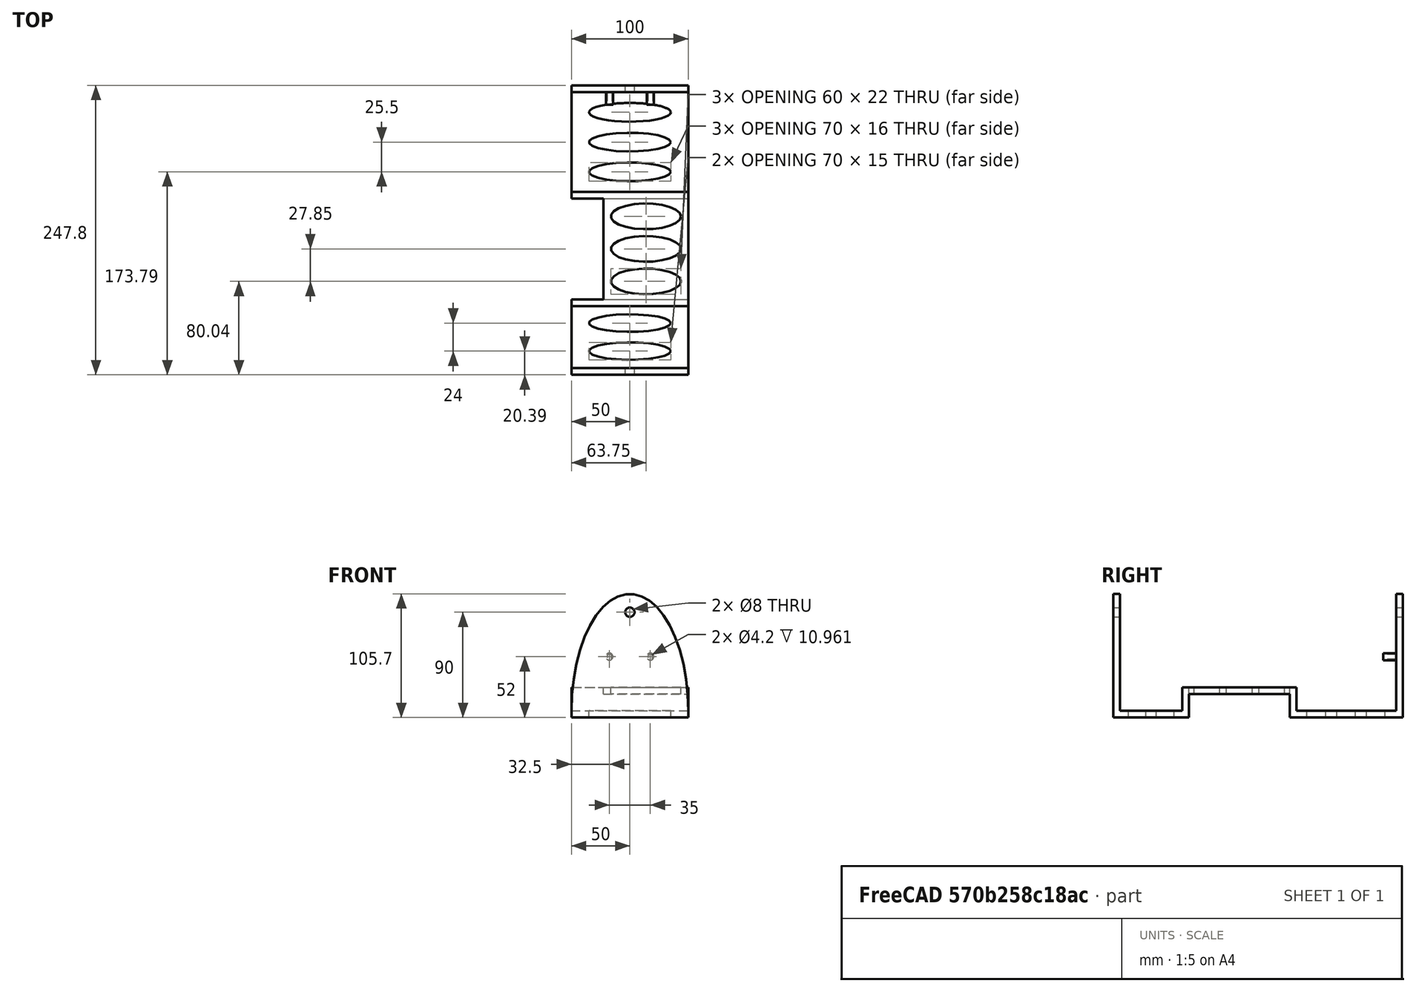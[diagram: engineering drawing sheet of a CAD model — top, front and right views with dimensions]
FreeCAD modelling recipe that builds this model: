
FCSTD DOCUMENT  (FreeCAD 0.16R6706 (Git))
Label: S2H-bottom-motor-coupling
License: All rights reserved
LicenseURL: http://en.wikipedia.org/wiki/All_rights_reserved
objects: Part::Ellipse×16, Part::Cut×12, Part::Loft×10, Part::Box×5, Part::Cylinder×5, Part::Feature×4, Part::MultiFuse×1
note: 53 computed .brp shape members not serialized (recipe doc carries the construction recipe); baked Part::Feature solids carry a one-line shape summary decoded from their .brp

FEATURE [Part::Box] Box  label="Cube"
  Height = 5.7
  Length = 72.5
  Placement = pos=(27.5,-5.7,20) rot=(0,0,1;0rad)
  Width = 86.4
  expr: Length = 100 - 27.5
FEATURE [Part::Box] Box001  label="Cube001"
  Height = 25.7
  Length = 100
  Placement = pos=(0,-11.4,0) rot=(0,0,1;0rad)
  Width = 5.7
  expr: Placement.Base.y = -2 * 5.7mm
FEATURE [Part::Box] Box002  label="Cube002"
  Height = 25.7
  Length = 100
  Placement = pos=(0,80.7,0) rot=(0,0,1;0rad)
  Width = 5.7
  expr: Placement.Base.y = 86.40000000000001 - 5.7
FEATURE [Part::Box] Box003  label="Cube003"
  Height = 5.7
  Length = 100
  Placement = pos=(0,86.4,0) rot=(0,0,1;0rad)
  Width = 91.0114
  expr: Placement.Base.y = 92.09999999999999 - 5.7
FEATURE [Part::Box] Box004  label="Cube004"
  Height = 5.7
  Length = 100
  Placement = pos=(0,-70.3886,0) rot=(0,0,1;0rad)
  Width = 58.9886
  expr: Placement.Base.y = -64.68859999999999 - 5.7
FEATURE [Part::Feature] Face002
  Placement = pos=(0,0,0) rot=(1,0,0;1.5708rad)
  shape: bbox 110 x 2e-07 x 110 mm, 1 faces, 0 solids (baked)
FEATURE [Part::Feature] Face003
  Placement = pos=(0,0,0) rot=(1,0,0;1.5708rad)
  shape: bbox 110 x 2e-07 x 110 mm, 1 faces, 0 solids (baked)
FEATURE [Part::Cylinder] Cylinder
  Angle = 360
  Height = 300
  Placement = pos=(50,-100,90) rot=(-1,0,0;1.5708rad)
  Radius = 4
FEATURE [Part::Loft] Loft
  Closed = false
  Placement = pos=(50,180.261,5.7) rot=(0,1,0;1.5708rad)
  Ruled = false
  Sections = -> [Face003,Face002]
  Solid = true
FEATURE [Part::Feature] Face004
  Placement = pos=(0,0,0) rot=(1,0,0;1.5708rad)
  shape: bbox 110 x 2e-07 x 110 mm, 1 faces, 0 solids (baked)
FEATURE [Part::Feature] Face005
  Placement = pos=(0,0,0) rot=(1,0,0;1.5708rad)
  shape: bbox 110 x 2e-07 x 110 mm, 1 faces, 0 solids (baked)
FEATURE [Part::Loft] Loft001
  Closed = false
  Placement = pos=(50,-61.8386,5.7) rot=(0,1,0;1.5708rad)
  Ruled = false
  Sections = -> [Face005,Face004]
  Solid = true
FEATURE [Part::Cut] Cut  label="holder tab back"
  Base = -> Loft001
  Placement = pos=(0,-2.85,0) rot=(0,0,1;0rad)
  Tool = -> Cylinder
  expr: Placement.Base.y = 2.85 - 5.7
FEATURE [Part::Cut] Cut001  label="holder tab front"
  Base = -> Loft
  Placement = pos=(0,-2.85,0) rot=(0,0,1;0rad)
  Tool = -> Cylinder
  expr: Placement.Base.y = 2.85 - 5.7
FEATURE [Part::Cylinder] Cylinder013
  Angle = 360
  Height = 12
  Radius = 2.1
FEATURE [Part::Cylinder] Cylinder014
  Angle = 360
  Height = 11
  Radius = 3
FEATURE [Part::Cut] Cut009
  Base = -> Cylinder014
  Placement = pos=(67.5,171.75,52) rot=(1,0,0;1.5708rad)
  Tool = -> Cylinder013
FEATURE [Part::Cylinder] Cylinder015
  Angle = 360
  Height = 12
  Radius = 2.1
FEATURE [Part::Cylinder] Cylinder016
  Angle = 360
  Height = 11
  Radius = 3
FEATURE [Part::Cut] Cut010
  Base = -> Cylinder016
  Placement = pos=(32.5,171.75,52) rot=(1,0,0;1.5708rad)
  Tool = -> Cylinder015
FEATURE [Part::Ellipse] Ellipse
  Angle0 = 0
  Angle1 = 360
  MajorRadius = 35
  MinorRadius = 7.5
FEATURE [Part::Ellipse] Ellipse001
  Angle0 = 0
  Angle1 = 360
  MajorRadius = 35
  MinorRadius = 8
  Placement = pos=(0,86.4,0) rot=(0,0,1;0rad)
FEATURE [Part::Ellipse] Ellipse002
  Angle0 = 0
  Angle1 = 360
  MajorRadius = 30
  MinorRadius = 11
FEATURE [Part::Ellipse] Ellipse003
  Angle0 = 0
  Angle1 = 360
  MajorRadius = 35
  MinorRadius = 7.5
  Placement = pos=(0,0,5.7) rot=(0,0,1;0rad)
FEATURE [Part::Loft] Loft002  label="back1"
  Closed = false
  Placement = pos=(50,-50,0) rot=(0,0,1;0rad)
  Ruled = false
  Sections = -> [Ellipse,Ellipse003]
  Solid = true
FEATURE [Part::Ellipse] Ellipse004
  Angle0 = 0
  Angle1 = 360
  MajorRadius = 30
  MinorRadius = 11
  Placement = pos=(0,0,5.7) rot=(0,0,1;0rad)
FEATURE [Part::Loft] Loft003  label="mid2"
  Closed = false
  Placement = pos=(63.75,37.5,20) rot=(0,0,1;0rad)
  Ruled = false
  Sections = -> [Ellipse002,Ellipse004]
  Solid = true
  expr: Placement.Base.y = -5.7 + 43.2
  expr: Placement.Base.x = 27.5 + 72.5 / 2
FEATURE [Part::Ellipse] Ellipse005
  Angle0 = 0
  Angle1 = 360
  MajorRadius = 35
  MinorRadius = 8
  Placement = pos=(0,86.4,5.7) rot=(0,0,1;0rad)
FEATURE [Part::Loft] Loft004  label="front1"
  Closed = false
  Placement = pos=(50,17,0) rot=(0,0,1;0rad)
  Ruled = false
  Sections = -> [Ellipse001,Ellipse005]
  Solid = true
FEATURE [Part::Ellipse] Ellipse006
  Angle0 = 0
  Angle1 = 360
  MajorRadius = 30
  MinorRadius = 11
FEATURE [Part::Ellipse] Ellipse007
  Angle0 = 0
  Angle1 = 360
  MajorRadius = 30
  MinorRadius = 11
  Placement = pos=(0,0,5.7) rot=(0,0,1;0rad)
FEATURE [Part::Loft] Loft005  label="mid1"
  Closed = false
  Placement = pos=(63.75,9.65,20) rot=(0,0,1;0rad)
  Ruled = false
  Sections = -> [Ellipse006,Ellipse007]
  Solid = true
  expr: Placement.Base.y = (37.5 - 12.5 - 5.7) / 2
  expr: Placement.Base.x = 27.5 + 72.5 / 2
FEATURE [Part::Ellipse] Ellipse008
  Angle0 = 0
  Angle1 = 360
  MajorRadius = 30
  MinorRadius = 11
FEATURE [Part::Ellipse] Ellipse009
  Angle0 = 0
  Angle1 = 360
  MajorRadius = 30
  MinorRadius = 11
  Placement = pos=(0,0,5.7) rot=(0,0,1;0rad)
FEATURE [Part::Loft] Loft006  label="mid3"
  Closed = false
  Placement = pos=(63.75,65.35,20) rot=(0,0,1;0rad)
  Ruled = false
  Sections = -> [Ellipse008,Ellipse009]
  Solid = true
  expr: Placement.Base.y = 37.5 + 12.5 + (36.4 - 5.7) / 2
  expr: Placement.Base.x = 27.5 + 72.5 / 2
FEATURE [Part::Cut] Cut011
  Base = -> Box
  Tool = -> Loft005
FEATURE [Part::Cut] Cut012
  Base = -> Cut011
  Tool = -> Loft003
FEATURE [Part::Cut] Cut013
  Base = -> Cut012
  Tool = -> Loft006
FEATURE [Part::Ellipse] Ellipse010
  Angle0 = 0
  Angle1 = 360
  MajorRadius = 35
  MinorRadius = 7.5
FEATURE [Part::Ellipse] Ellipse011
  Angle0 = 0
  Angle1 = 360
  MajorRadius = 35
  MinorRadius = 7.5
  Placement = pos=(0,0,5.7) rot=(0,0,1;0rad)
FEATURE [Part::Loft] Loft007  label="back2"
  Closed = false
  Placement = pos=(50,-26,0) rot=(0,0,1;0rad)
  Ruled = false
  Sections = -> [Ellipse010,Ellipse011]
  Solid = true
FEATURE [Part::Ellipse] Ellipse012
  Angle0 = 0
  Angle1 = 360
  MajorRadius = 35
  MinorRadius = 8
  Placement = pos=(0,86.4,0) rot=(0,0,1;0rad)
FEATURE [Part::Ellipse] Ellipse013
  Angle0 = 0
  Angle1 = 360
  MajorRadius = 35
  MinorRadius = 8
  Placement = pos=(0,86.4,5.7) rot=(0,0,1;0rad)
FEATURE [Part::Loft] Loft008  label="front002"
  Closed = false
  Placement = pos=(50,42.5,0) rot=(0,0,1;0rad)
  Ruled = false
  Sections = -> [Ellipse012,Ellipse013]
  Solid = true
FEATURE [Part::Ellipse] Ellipse014
  Angle0 = 0
  Angle1 = 360
  MajorRadius = 35
  MinorRadius = 8
  Placement = pos=(0,86.4,0) rot=(0,0,1;0rad)
FEATURE [Part::Ellipse] Ellipse015
  Angle0 = 0
  Angle1 = 360
  MajorRadius = 35
  MinorRadius = 8
  Placement = pos=(0,86.4,5.7) rot=(0,0,1;0rad)
FEATURE [Part::Loft] Loft009  label="front003"
  Closed = false
  Placement = pos=(50,68,0) rot=(0,0,1;0rad)
  Ruled = false
  Sections = -> [Ellipse014,Ellipse015]
  Solid = true
FEATURE [Part::Cut] Cut014
  Base = -> Box004
  Tool = -> Loft002
FEATURE [Part::Cut] Cut015
  Base = -> Cut014
  Tool = -> Loft007
FEATURE [Part::Cut] Cut016
  Base = -> Box003
  Tool = -> Loft004
FEATURE [Part::Cut] Cut017
  Base = -> Cut016
  Tool = -> Loft008
FEATURE [Part::Cut] Cut018
  Base = -> Cut017
  Tool = -> Loft009
FEATURE [Part::MultiFuse] Fusion
  Shapes = -> [Box001,Box002,Cut,Cut001,Cut009,Cut010,Cut013,Cut015,Cut018]
